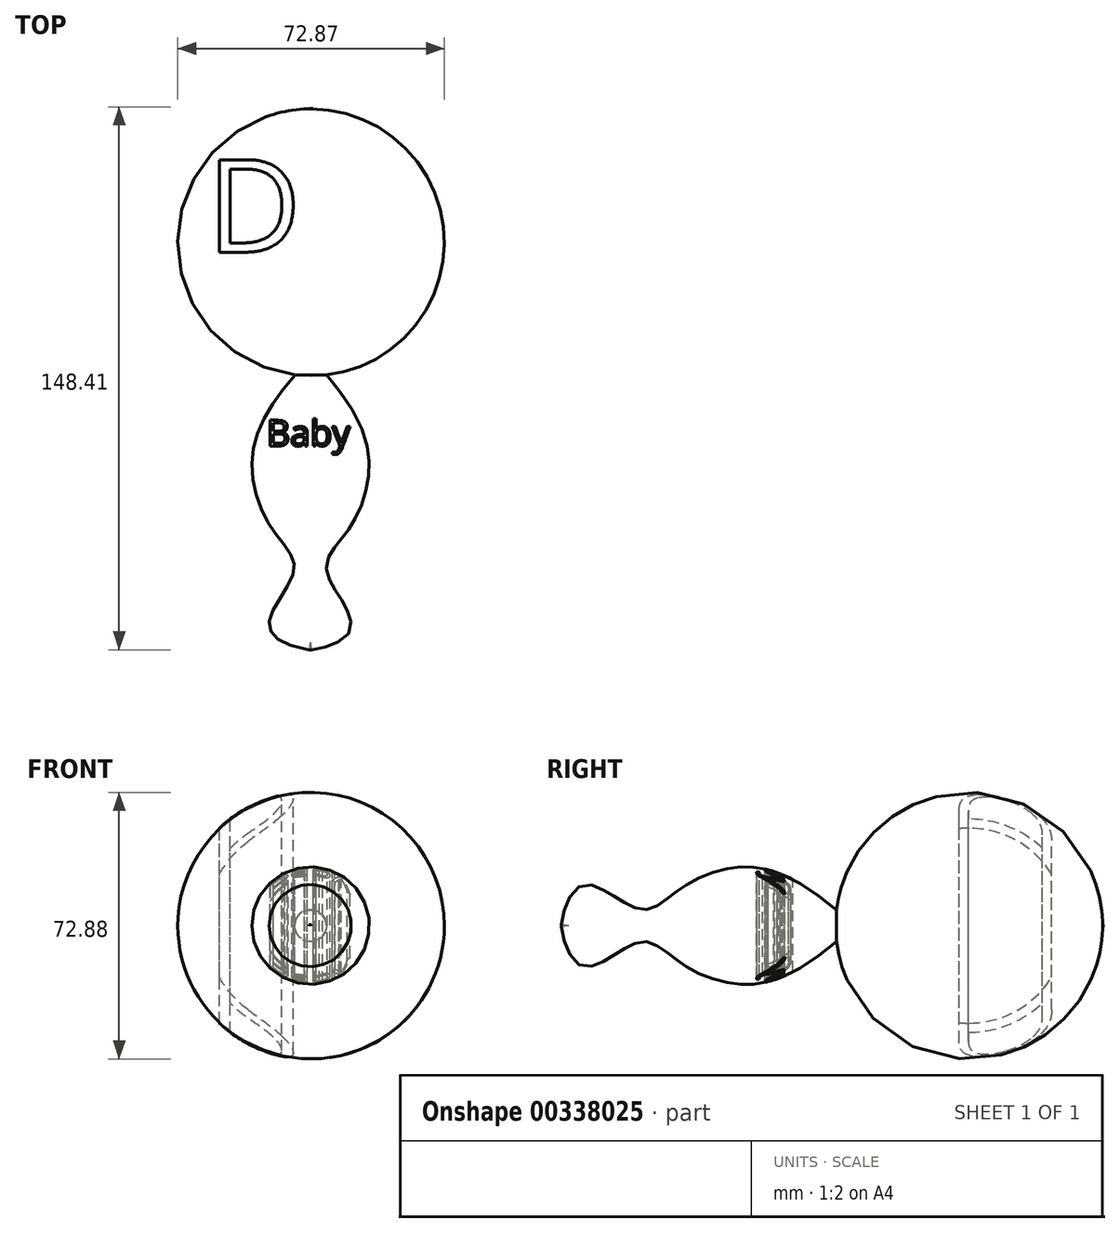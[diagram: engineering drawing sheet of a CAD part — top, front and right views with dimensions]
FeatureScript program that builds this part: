
annotation { "Feature Type Name" : "Feature", "Feature Type Description" : "" }
export const myFeature = defineFeature(function(context is Context, id is Id, definition is map)
    precondition{}
    {
        {
            var Q0;
            Q0=qCreatedBy(makeId("Top.planeOp"),FACE);
            var sketch = newSketch(context, id + "F0", { "sketchPlane" : qUnion([Q0])});
            skLineSegment(sketch, "E0", {"start": v(0, 74.82) * mm, "end": v(0, 74.32) * mm});
            skLineSegment(sketch, "E1", {"start": v(0, 0) * mm, "end": v(0, 3.52) * mm});
            skLineSegment(sketch, "E2", {"start": v(0, 0.5) * mm, "end": v(0, 0.5) * mm});
            skLineSegment(sketch, "E3", {"start": v(0, 0.5) * mm, "end": v(0, 0) * mm});
            skArc(sketch, "E4", {"start": v(4.17, 1.54) * mm, "mid": v(36.45, 39.9) * mm, "end": v(0, 74.32) * mm});
            skFitSpline(sketch, "E5", {"points": [v(4.17, 1.54) * mm, v(15.8, -21.23) * mm, v(10, -40.9) * mm, v(4.17, -51.67) * mm, v(10.87, -65.78) * mm, v(0, -73.59) * mm], "startDerivative": vector(77.74, -90.75) * mm, "endDerivative": vector(-134.18, -20.59) * mm});
            skFitSpline(sketch, "E6.0", {"points": [v(2.66, 0.23) * mm, v(4.24, -1.62) * mm, v(7.2, -5.33) * mm, v(10.1, -9.95) * mm, v(11.86, -13.63) * mm, v(12.87, -16.39) * mm, v(13.44, -18.68) * mm, v(13.72, -20.51) * mm, v(13.89, -22.35) * mm, v(13.87, -24.68) * mm, v(13.52, -27.49) * mm, v(12.88, -30.27) * mm, v(11.98, -32.98) * mm, v(11.05, -35.13) * mm, v(10.21, -36.77) * mm, v(9.54, -37.95) * mm, v(8.83, -39.08) * mm, v(8.1, -40.14) * mm, v(7.33, -41.17) * mm, v(6.27, -42.51) * mm, v(4.94, -44.17) * mm, v(3.74, -45.88) * mm, v(2.94, -47.37) * mm, v(2.47, -48.57) * mm, v(2.17, -49.87) * mm, v(2.1, -51.02) * mm, v(2.18, -51.97) * mm, v(2.35, -52.9) * mm, v(2.68, -54.03) * mm, v(3.22, -55.34) * mm, v(3.87, -56.63) * mm, v(4.6, -57.9) * mm, v(5.6, -59.55) * mm, v(6.86, -61.55) * mm, v(7.92, -63.4) * mm, v(8.52, -64.73) * mm, v(8.77, -65.46) * mm, v(8.88, -65.96) * mm, v(8.95, -66.4) * mm, v(8.94, -66.9) * mm, v(8.84, -67.4) * mm, v(8.62, -67.87) * mm, v(8.27, -68.36) * mm, v(7.54, -69.06) * mm, v(6.09, -69.96) * mm, v(3.41, -70.91) * mm, v(1.03, -71.4) * mm, v(-0.3, -71.6) * mm]});
            skArc(sketch, "E7.0", {"start": v(3.95, 3.52) * mm, "mid": v(34.46, 39.78) * mm, "end": v(0, 72.32) * mm});
            skLineSegment(sketch, "E8", {"start": v(0, 74.32) * mm, "end": v(0, 72.32) * mm});
            skLineSegment(sketch, "E9", {"start": v(3.95, 3.52) * mm, "end": v(0, 3.52) * mm});
            skLineSegment(sketch, "E10", {"start": v(0, 3.52) * mm, "end": v(0, 0.5) * mm});
            skLineSegment(sketch, "E11", {"start": v(3.07, -0.25) * mm, "end": v(0, 0.5) * mm});
            skLineSegment(sketch, "E12", {"start": v(-0.3, -71.6) * mm, "end": v(0, -73.59) * mm});
            skLineSegment(sketch, "E13", {"start": v(0, 74.82) * mm, "end": v(-0.3, -71.6) * mm});
            skSolve(sketch);
        }
        {
            var Q0;
            Q0=makeQuery(id+"F0.imprint","IMPRINT",FACE,{"disambiguationData":[TD([[makeQuery(id+"F0.imprint","IMPRINT",EDGE,{"derivedFrom":sQuery(id+"F0.wireOp",EDGE,"E4")}),1.0]])]});
            var Q1;
            Q1=makeQuery(id+"F0.imprint","IMPRINT",FACE,{"disambiguationData":[TD([[makeQuery(id+"F0.imprint","IMPRINT",EDGE,{"derivedFrom":sQuery(id+"F0.wireOp",EDGE,"E0")}),-1.0]])]});
            var Q2;
            Q2=sQuery(id+"F0.wireOp",EDGE,"E13");
            revolve(context, id + "F1", {"entities" : qUnion([Q0, Q1]), "axis" : qUnion([Q2]), "revolveType" : RevolveType.FULL});
        }
        {
            var Q0;
            Q0=qCreatedBy(makeId("Top.planeOp"),FACE);
            var sketch = newSketch(context, id + "F2", { "sketchPlane" : qUnion([Q0])});
            skText(sketch, "E14", { "text": "D", "fontName": "OpenSans-Regular.ttf"});
            skText(sketch, "E15", { "text": "M", "fontName": "OpenSans-Regular.ttf"});
            skCircle(sketch, "E16", {"center": v(-7.93, 26.34) * mm, "radius": 4.61 * mm});
            skCircle(sketch, "E17", {"center": v(-9.63, 11.05) * mm, "radius": 4.82 * mm});
            skCircle(sketch, "E18", {"center": v(-25.21, 24.93) * mm, "radius": 5.1 * mm});
            skCircle(sketch, "E19", {"center": v(7.93, 44.76) * mm, "radius": 5.13 * mm});
            skCircle(sketch, "E20", {"center": v(8.5, 64.59) * mm, "radius": 4.82 * mm});
            skCircle(sketch, "E21", {"center": v(24.36, 49.86) * mm, "radius": 4.82 * mm});
            skText(sketch, "E22", { "text": "Baby", "fontName": "OpenSans-Regular.ttf"});
            const initialGuessF2  = {"E14": [-0.02861, 0.03513, 1, 0, 0.0255], "E15": [0, 0.01303, 1, 0, 0.02266], "E22": [-0.01218, -0.01785, 1, 0, 0.00708]};
            skSetInitialGuess(sketch, initialGuessF2);
            skSolve(sketch);
        }
        {
            var Q0;
            Q0 = qSketchRegion(id + "F2", true);
            extrude(context, id + "F3", {"entities" : qUnion([Q0]), "operationType" : NewBodyOperationType.REMOVE, "oppositeDirection" : true, "depth" : 400 * mm, "symmetric" : true});
        }
    });
